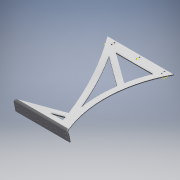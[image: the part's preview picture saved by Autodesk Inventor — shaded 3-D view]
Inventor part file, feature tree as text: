
AUTODESK INVENTOR PART (.ipt)
format: ipt  version: 2016 (Build 200138000, 138)  size: 228,864 bytes
history: native  units: mm
features: sheet_metal_op x4, sketch x4, reference x4, other x2, plane x1, extrude x1, projected_geometry x1
ambient origin geometry x8: Origin, YZ Plane, XZ Plane, XY Plane, X Axis, Y Axis, Z Axis, Center Point
bodies: Solid1 (feature_tree)
feature tree (17):
  plane  "Work Plane1"
  sheet_metal_op  "Face1"
  sketch  "Sketch3"  dims[d9=500.0mm]
  extrude  "Extrusion1"  Depth=50.0mm
  sheet_metal_op  "Face2"
  sheet_metal_op  "Bend3"
  sketch  "Sketch1"  dims[d6=5.0mm d8=50.0mm]
  reference  "Reference1"
  other  "Plate1"
  reference  "Reference2"
  sketch  "Sketch4"  dims[d11=2000.0mm]
  reference  "Reference4"
  projected_geometry  "Projected Loop2"
  sketch  "Sketch10"  dims[d15=30.0mm d16=30.0mm d17=30.0mm d18=10.0mm d19=0.0mm d21=3.490659mm d22=30.0mm d23=30.0mm d34=5.0mm d35=5.0mm d36=2.5mm d37=10.0mm d38=5.0mm d39=5.0mm d40=2.5mm d41=10.0mm d42=5.0mm d43=5.0mm]
  reference  "Reference17"
  other  "Plate3"
  sheet_metal_op  "Bend2"
